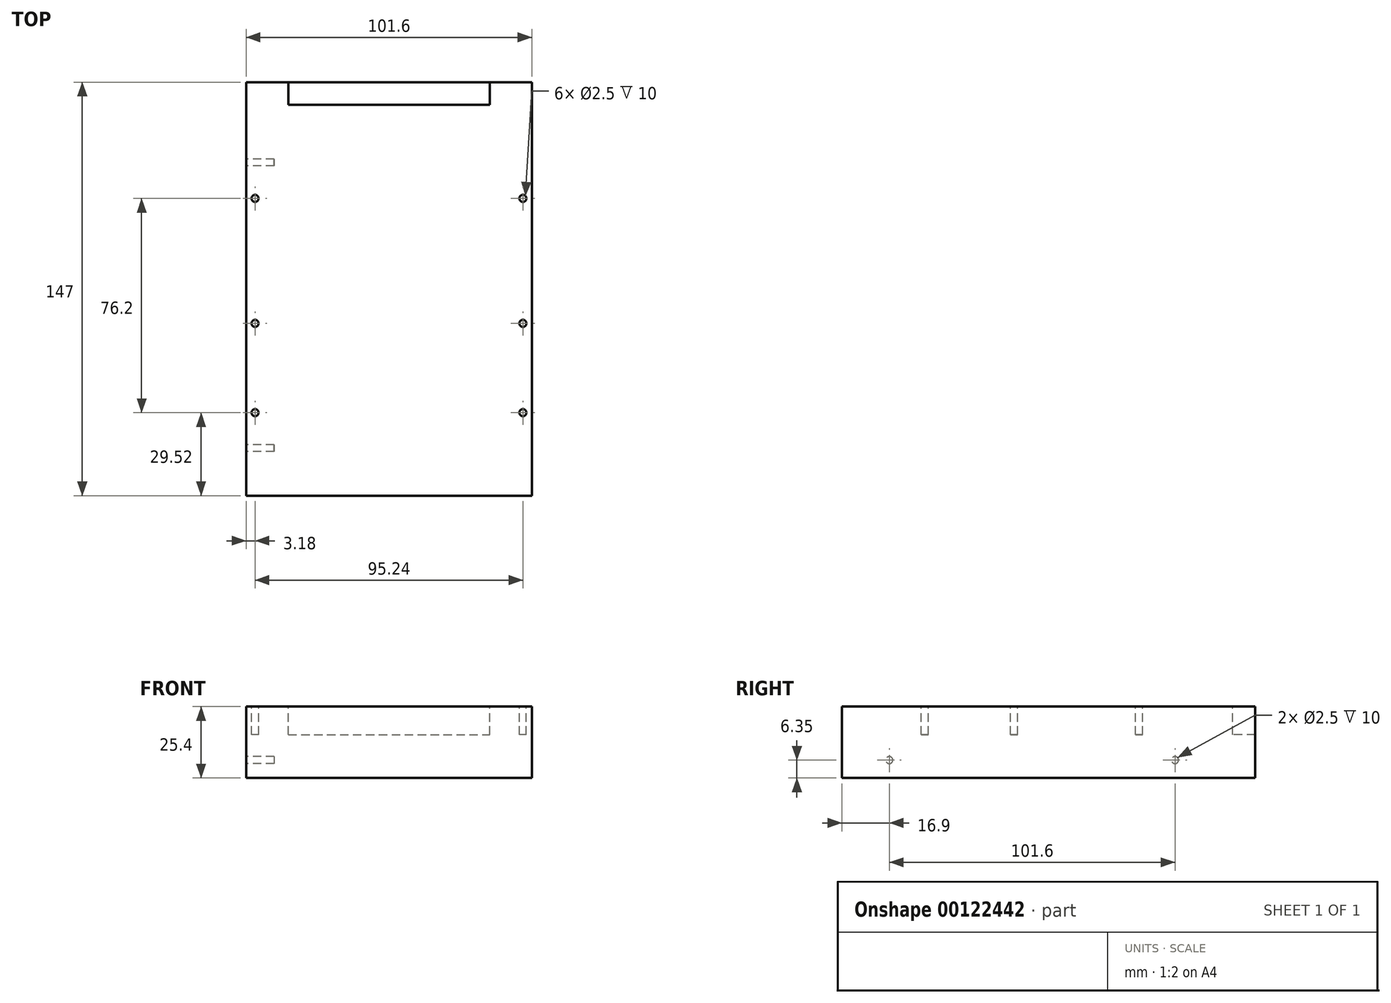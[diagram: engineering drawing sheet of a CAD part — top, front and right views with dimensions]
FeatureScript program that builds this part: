
annotation { "Feature Type Name" : "Feature", "Feature Type Description" : "" }
export const myFeature = defineFeature(function(context is Context, id is Id, definition is map)
    precondition{}
    {
        {
            var Q0;
            Q0=qCreatedBy(makeId("Top.planeOp"),FACE);
            var sketch = newSketch(context, id + "F0", { "sketchPlane" : qUnion([Q0])});
            skLineSegment(sketch, "E0.bottom", {"start": v(0, 0) * mm, "end": v(101.6, 0) * mm});
            skLineSegment(sketch, "E0.top", {"start": v(0, 147) * mm, "end": v(101.6, 147) * mm});
            skLineSegment(sketch, "E0.left", {"start": v(0, 0) * mm, "end": v(0, 147) * mm});
            skLineSegment(sketch, "E0.right", {"start": v(101.6, 0) * mm, "end": v(101.6, 147) * mm});
            skSolve(sketch);
        }
        {
            var Q0;
            Q0 = qSketchRegion(id + "F0", true);
            extrude(context, id + "F1", {"entities" : qUnion([Q0]), "depth" : 25.4 * mm});
        }
        {
            var Q0;
            Q0=makeQuery(id+"F1.opExtrude","CAP_FACE",FACE,{"disambiguationData":[OSD([sQuery(id+"F0.wireOp",EDGE,"E0.bottom"),sQuery(id+"F0.wireOp",EDGE,"E0.top"),sQuery(id+"F0.wireOp",EDGE,"E0.left"),sQuery(id+"F0.wireOp",EDGE,"E0.right")])],"isStart":false});
            var sketch = newSketch(context, id + "F2", { "sketchPlane" : qUnion([Q0])});
            skCircle(sketch, "E1", {"center": v(3.18, 29.52) * mm, "radius": 1.25 * mm});
            skCircle(sketch, "E2", {"center": v(3.18, 61.27) * mm, "radius": 1.25 * mm});
            skCircle(sketch, "E3", {"center": v(3.18, 105.72) * mm, "radius": 1.25 * mm});
            skLineSegment(sketch, "E4", {"start": v(50.8, 147) * mm, "end": v(50.8, 0) * mm, "construction": true});
            skCircle(sketch, "E5.MirrorC", {"center": v(98.42, 29.52) * mm, "radius": 1.25 * mm});
            skCircle(sketch, "E6.MirrorC", {"center": v(98.42, 61.27) * mm, "radius": 1.25 * mm});
            skCircle(sketch, "E7.MirrorC", {"center": v(98.42, 105.72) * mm, "radius": 1.25 * mm});
            skLineSegment(sketch, "E8.bottom", {"start": v(15, 147) * mm, "end": v(86.6, 147) * mm});
            skLineSegment(sketch, "E8.top", {"start": v(15, 139) * mm, "end": v(86.6, 139) * mm});
            skLineSegment(sketch, "E8.left", {"start": v(15, 147) * mm, "end": v(15, 139) * mm});
            skLineSegment(sketch, "E8.right", {"start": v(86.6, 147) * mm, "end": v(86.6, 139) * mm});
            skSolve(sketch);
        }
        {
            var Q0;
            Q0 = qSketchRegion(id + "F2", true);
            extrude(context, id + "F3", {"entities" : qUnion([Q0]), "operationType" : NewBodyOperationType.REMOVE, "oppositeDirection" : true, "depth" : 10 * mm});
        }
        {
            var Q0;
            Q0=makeQuery(id+"F1.opExtrude","SWEPT_FACE",FACE,{"disambiguationData":[OSD([sQuery(id+"F0.wireOp",EDGE,"E0.left")])]});
            var sketch = newSketch(context, id + "F4", { "sketchPlane" : qUnion([Q0])});
            skCircle(sketch, "E9", {"center": v(-118.5, 6.35) * mm, "radius": 1.25 * mm});
            skCircle(sketch, "E10", {"center": v(-16.9, 6.35) * mm, "radius": 1.25 * mm});
            skSolve(sketch);
        }
        {
            var Q0;
            Q0 = qSketchRegion(id + "F4", true);
            extrude(context, id + "F5", {"entities" : qUnion([Q0]), "operationType" : NewBodyOperationType.REMOVE, "oppositeDirection" : true, "depth" : 10 * mm});
        }
        {
            var Q0;
            Q0=makeQuery(id+"F1.opExtrude","SWEPT_FACE",FACE,{"disambiguationData":[OSD([sQuery(id+"F0.wireOp",EDGE,"E0.left")])]});
            var Q1;
            Q1=makeQuery(id+"F1.opExtrude","SWEPT_FACE",FACE,{"disambiguationData":[OSD([sQuery(id+"F0.wireOp",EDGE,"E0.right")])]});
            cPlane(context, id + "F6", {"entities" : qUnion([Q0, Q1]), "cplaneType" : CPlaneType.MID_PLANE, "offset" : 25 * mm, "width" : 150 * mm, "height" : 150 * mm});
        }
    });
